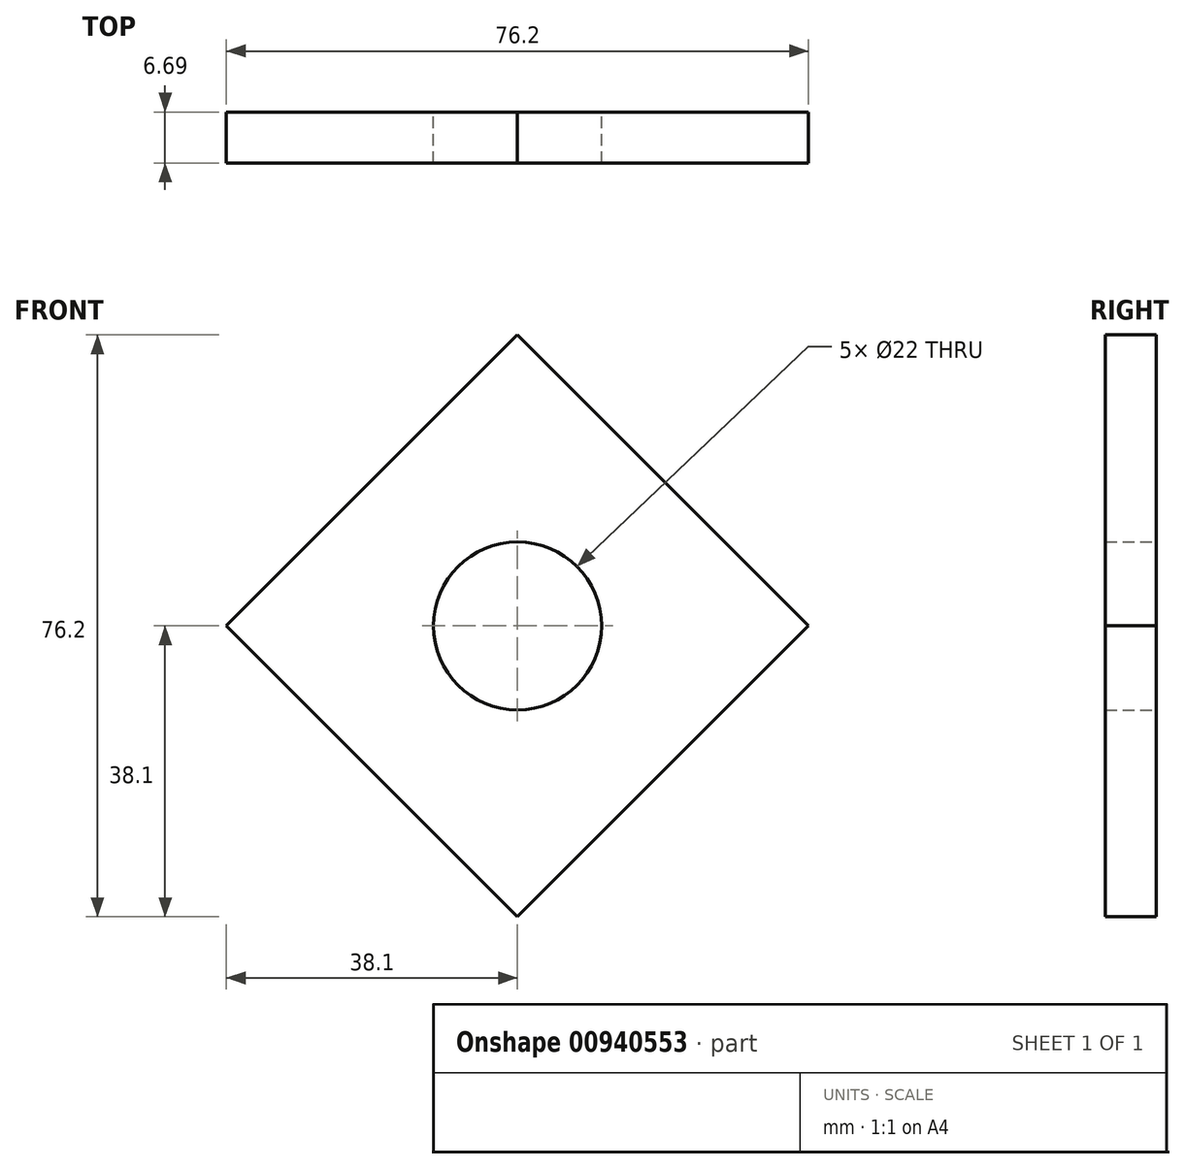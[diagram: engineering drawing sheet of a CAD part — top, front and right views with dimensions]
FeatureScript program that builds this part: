
annotation { "Feature Type Name" : "Feature", "Feature Type Description" : "" }
export const myFeature = defineFeature(function(context is Context, id is Id, definition is map)
    precondition{}
    {
        {
            var Q0;
            Q0=qCreatedBy(makeId("Front.planeOp"),FACE);
            var sketch = newSketch(context, id + "F0", { "sketchPlane" : qUnion([Q0])});
            skCircle(sketch, "E0", {"center": v(0, 0) * mm, "radius": 11 * mm});
            skPoint(sketch, "E1.0.midPoint", {"position": v(30.26, 52.42) * mm});
            skLineSegment(sketch, "E2", {"start": v(-60.53, 0) * mm, "end": v(60.53, 0) * mm});
            skLineSegment(sketch, "E3", {"start": v(0, 0) * mm, "end": v(-38.1, 0) * mm});
            skLineSegment(sketch, "E4", {"start": v(-38.1, 0) * mm, "end": v(0, 38.1) * mm});
            skLineSegment(sketch, "E5", {"start": v(0, 38.1) * mm, "end": v(38.1, 0) * mm});
            skLineSegment(sketch, "E6", {"start": v(38.1, 0) * mm, "end": v(0, -38.1) * mm});
            skLineSegment(sketch, "E7", {"start": v(0, -38.1) * mm, "end": v(-38.1, 0) * mm});
            skPoint(sketch, "E8.orphan", {"position": v(60.53, 34.95) * mm});
            skPoint(sketch, "E9.orphan", {"position": v(60.53, -34.95) * mm});
            skPoint(sketch, "E10.start.orphan", {"position": v(0, 69.9) * mm});
            skPoint(sketch, "E11.orphan", {"position": v(-60.53, -34.95) * mm});
            skSolve(sketch);
        }
        {
            var Q0;
            Q0 = qSketchRegion(id + "F0", true);
            extrude(context, id + "F1", {"entities" : qUnion([Q0]), "depth" : 6.7 * mm, "offsetDistance" : 25 * mm});
        }
    });
